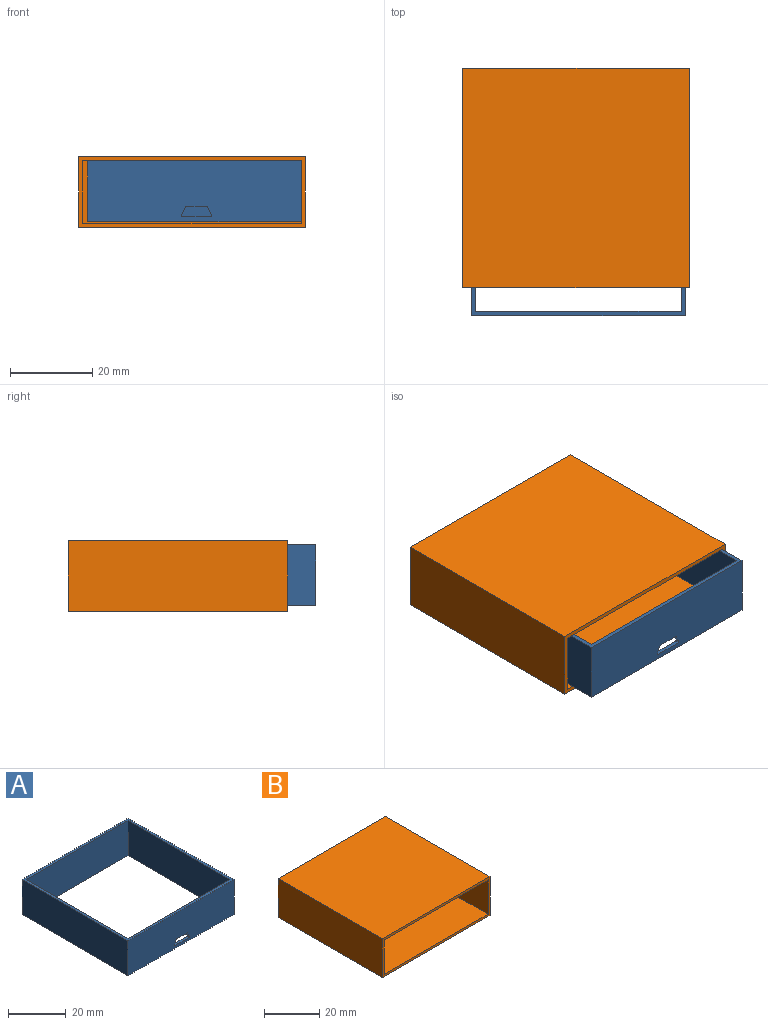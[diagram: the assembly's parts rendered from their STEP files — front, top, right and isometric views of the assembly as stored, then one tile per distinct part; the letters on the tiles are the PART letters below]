
ASSEMBLY  parts=2 mates=1
PART A: 18 faces, bbox 52x52x14.8 mm
  f0: plane 52x14.8mm, normal (0,1,0), area 769.6mm2, adj f1,f7,f8,f9
  f1: plane 52x14.8mm, normal (-1,0,0), area 769.6mm2, adj f0,f2,f8,f9
  f2: plane 52x14.8mm, normal (0,-1,0), area 754.1mm2, adj f1,f7,f8,f9,f10,f11,f12,f13
  f3: plane 50x14.8mm, normal (-1,0,0), area 740mm2, adj f4,f6,f8,f9
  f4: plane 50x14.8mm, normal (0,1,0), area 724.5mm2, adj f3,f5,f8,f9,f10,f11,f12,f13
  f5: plane 50x14.8mm, normal (1,0,0), area 740mm2, adj f4,f6,f8,f9
  f6: plane 50x14.8mm, normal (0,-1,0), area 740mm2, adj f3,f5,f8,f9
  f7: plane 52x14.8mm, normal (1,0,0), area 769.6mm2, adj f0,f2,f8,f9
  f8: plane 52x52mm, normal (0,0,1), area 204mm2, adj f0,f1,f2,f3,f4,f5,f6,f7
  f9: plane 52x52mm, normal (0,0,-1), area 204mm2, adj f0,f1,f2,f3,f4,f5,f6,f7
  f10: plane 1.95x1mm, normal (0.89,0,-0.45), area 2.2mm2, adj f2,f4,f14,f15
  f11: plane 5.16x1mm, normal (0,0,-1), area 5.2mm2, adj f2,f4,f14,f16
  f12: plane 7.15x1mm, normal (0,0,1), area 7.1mm2, adj f2,f4,f15,f17
  f13: plane 1.95x1mm, normal (-0.89,0,-0.45), area 2.2mm2, adj f2,f4,f16,f17
  f14: cylinder r=0.2mm len=1mm, axis (0,-1,0), area 0.2mm2, adj f2,f4,f10,f11
  f15: cylinder r=0.2mm len=1mm, axis (0,-1,0), area 0.4mm2, adj f2,f4,f10,f12
  f16: cylinder r=0.2mm len=1mm, axis (0,1,0), area 0.2mm2, adj f2,f4,f11,f13
  f17: cylinder r=0.2mm len=1mm, axis (0,1,0), area 0.4mm2, adj f2,f4,f12,f13
PART B: 11 faces, bbox 55.2x53.4x17.2 mm
  f0: plane 53.2x51.9mm, normal (0,0,1), area 2761.1mm2, adj f1,f7,f8,f10
  f1: plane 51.9x15.2mm, normal (1,0,0), area 788.9mm2, adj f0,f2,f8,f10
  f2: plane 53.2x51.9mm, normal (0,0,-1), area 2761.1mm2, adj f1,f7,f8,f10
  f3: plane 53.4x17.2mm, normal (1,0,0), area 918.5mm2, adj f4,f6,f8,f9
  f4: plane 55.2x53.4mm, normal (0,0,1), area 2947.7mm2, adj f3,f5,f8,f9
  f5: plane 53.4x17.2mm, normal (-1,0,0), area 918.5mm2, adj f4,f6,f8,f9
  f6: plane 55.2x53.4mm, normal (0,0,-1), area 2947.7mm2, adj f3,f5,f8,f9
  f7: plane 51.9x15.2mm, normal (-1,0,0), area 788.9mm2, adj f0,f2,f8,f10
  f8: plane 55.2x17.2mm, normal (0,-1,0), area 140.8mm2, adj f0,f1,f2,f3,f4,f5,f6,f7
  f9: plane 55.2x17.2mm, normal (0,1,0), area 949.4mm2, adj f3,f4,f5,f6
  f10: plane 53.2x15.2mm, normal (0,-1,0), area 808.6mm2, adj f0,f1,f2,f7
PLACE A t=(1.27,13.2,-15.39)mm
PLACE B t=(16.37,27.64,-9.38)mm
MATE slider B.f8 <-> A.f2  axis (0,-1,0) through (49.57,-25.76,-0.59)mm
